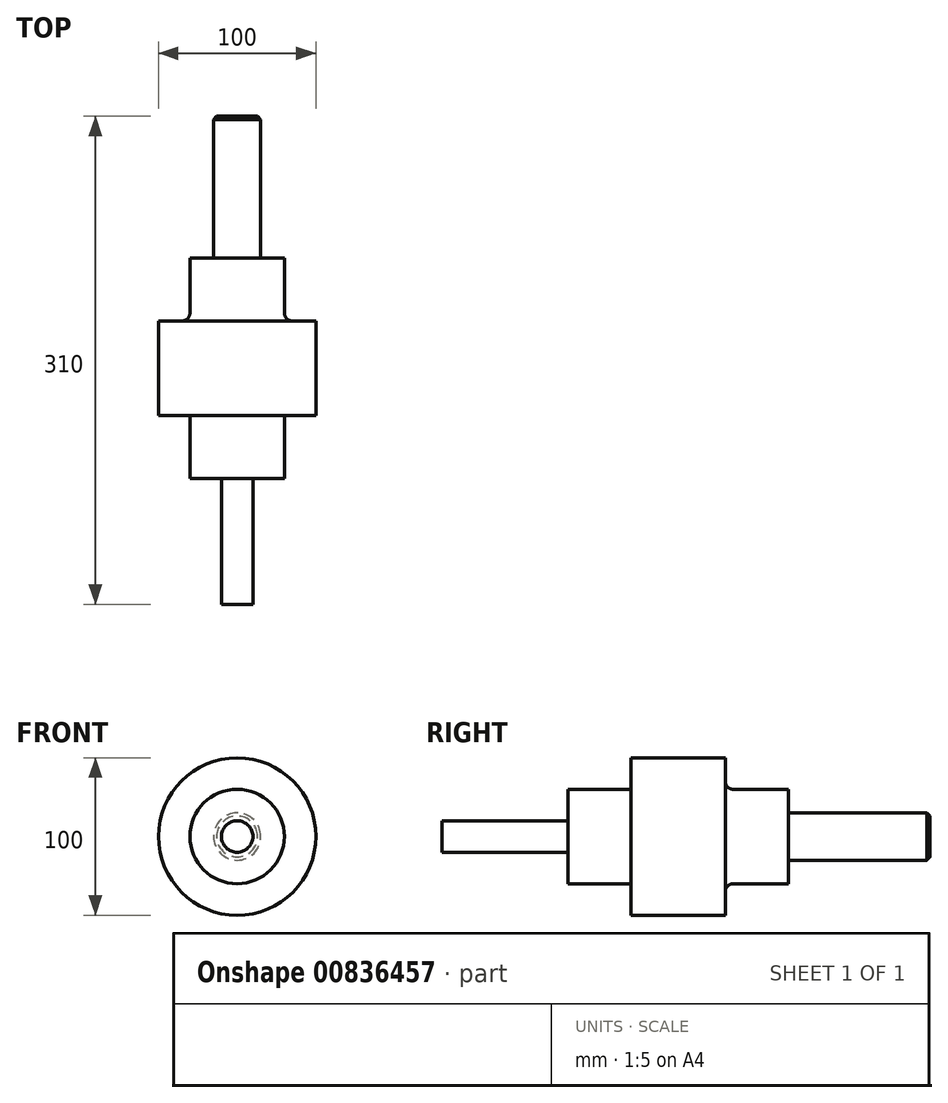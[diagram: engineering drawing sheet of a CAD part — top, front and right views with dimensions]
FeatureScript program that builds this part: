
annotation { "Feature Type Name" : "Feature", "Feature Type Description" : "" }
export const myFeature = defineFeature(function(context is Context, id is Id, definition is map)
    precondition{}
    {
        {
            var Q0;
            Q0=qCreatedBy(makeId("Top.planeOp"),FACE);
            var sketch = newSketch(context, id + "F0", { "sketchPlane" : qUnion([Q0])});
            skLineSegment(sketch, "E0", {"start": v(0, 190) * mm, "end": v(15, 190) * mm});
            skLineSegment(sketch, "E1", {"start": v(15, 190) * mm, "end": v(15, 100) * mm});
            skLineSegment(sketch, "E2", {"start": v(15, 100) * mm, "end": v(30, 100) * mm});
            skLineSegment(sketch, "E3", {"start": v(30, 100) * mm, "end": v(30, 60) * mm});
            skLineSegment(sketch, "E4", {"start": v(30, 60) * mm, "end": v(50, 60) * mm});
            skLineSegment(sketch, "E5", {"start": v(50, 60) * mm, "end": v(50, 0) * mm});
            skLineSegment(sketch, "E6", {"start": v(50, 0) * mm, "end": v(30, 0) * mm});
            skLineSegment(sketch, "E7", {"start": v(30, 0) * mm, "end": v(30, -40) * mm});
            skLineSegment(sketch, "E8", {"start": v(30, -40) * mm, "end": v(10, -40) * mm});
            skLineSegment(sketch, "E9", {"start": v(10, -40) * mm, "end": v(10, -120) * mm});
            skLineSegment(sketch, "E10", {"start": v(10, -120) * mm, "end": v(0, -120) * mm});
            skLineSegment(sketch, "E11", {"start": v(0, -120) * mm, "end": v(0, 190) * mm});
            skSolve(sketch);
        }
        {
            var Q0;
            Q0=makeQuery(id+"F0.imprint","IMPRINT",FACE,{"disambiguationData":[TD([[makeQuery(id+"F0.imprint","IMPRINT",EDGE,{"derivedFrom":sQuery(id+"F0.wireOp",EDGE,"E0")}),-1.0]])]});
            var Q1;
            Q1=sQuery(id+"F0.wireOp",EDGE,"E11");
            revolve(context, id + "F1", {"surfaceOperationType" : NewSurfaceOperationType.NEW, "entities" : qUnion([Q0]), "axis" : qUnion([Q1]), "revolveType" : RevolveType.FULL});
        }
        {
            var Q0;
            Q0=makeQuery(id+"F1.opRevolve","SWEPT_EDGE",EDGE,{"disambiguationData":[OSD([sQuery(id+"F0.wireOp",EDGE,"E3"),sQuery(id+"F0.wireOp",EDGE,"E4")])]});
            fillet(context, id + "F2", {"entities" : qUnion([Q0]), "radius" : 5 * mm, "tangentPropagation" : true, "allowEdgeOverflow" : false});
        }
        {
            var Q0;
            Q0=makeQuery(id+"F1.opRevolve","SWEPT_EDGE",EDGE,{"disambiguationData":[OSD([sQuery(id+"F0.wireOp",EDGE,"E0"),sQuery(id+"F0.wireOp",EDGE,"E1")])]});
            chamfer(context, id + "F3", {"entities" : qUnion([Q0]), "width" : 2 * mm, "tangentPropagation" : true});
        }
    });
